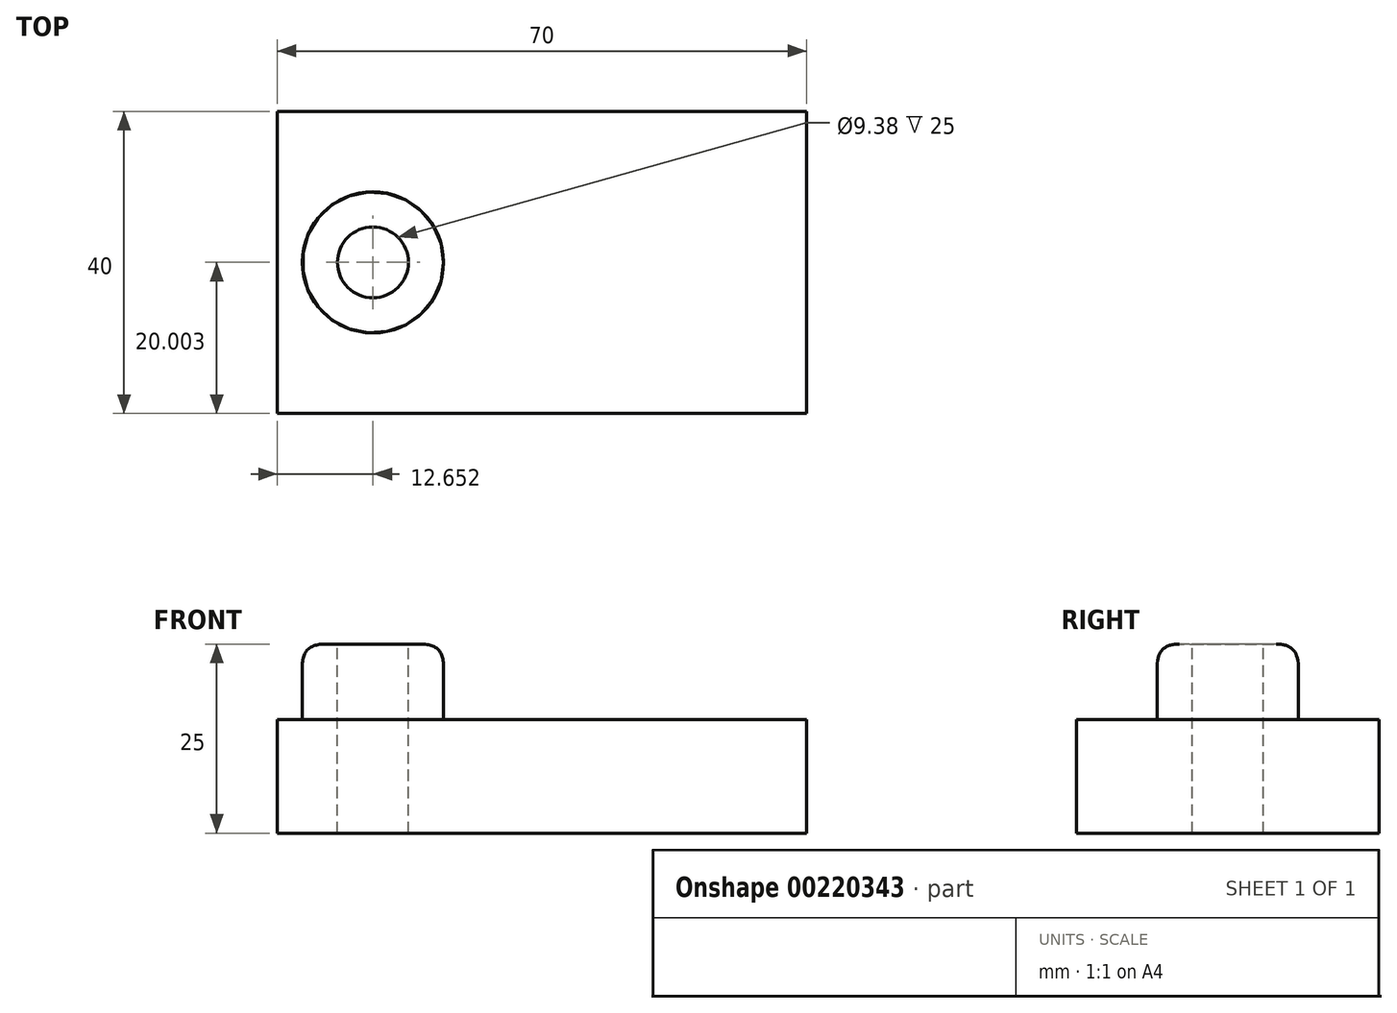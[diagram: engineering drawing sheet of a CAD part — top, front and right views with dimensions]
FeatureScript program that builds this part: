
annotation { "Feature Type Name" : "Feature", "Feature Type Description" : "" }
export const myFeature = defineFeature(function(context is Context, id is Id, definition is map)
    precondition{}
    {
        {
            var Q0;
            Q0=qCreatedBy(makeId("Top.planeOp"),FACE);
            var sketch = newSketch(context, id + "F0", { "sketchPlane" : qUnion([Q0])});
            skLineSegment(sketch, "E0.bottom", {"start": v(-41, 23.95) * mm, "end": v(29, 23.95) * mm});
            skLineSegment(sketch, "E0.top", {"start": v(-41, -16.05) * mm, "end": v(29, -16.05) * mm});
            skLineSegment(sketch, "E0.left", {"start": v(-41, 23.95) * mm, "end": v(-41, -16.05) * mm});
            skLineSegment(sketch, "E0.right", {"start": v(29, 23.95) * mm, "end": v(29, -16.05) * mm});
            skSolve(sketch);
        }
        {
            var Q0;
            Q0=makeQuery(id+"F0.imprint","IMPRINT",FACE,{"disambiguationData":[TD([[makeQuery(id+"F0.imprint","IMPRINT",EDGE,{"derivedFrom":sQuery(id+"F0.wireOp",EDGE,"E0.bottom")}),-1.0]])]});
            extrude(context, id + "F1", {"entities" : qUnion([Q0]), "depth" : 15 * mm});
        }
        {
            var Q0;
            Q0=makeQuery(id+"F1.opExtrude","CAP_FACE",FACE,{"disambiguationData":[OSD([sQuery(id+"F0.wireOp",EDGE,"E0.bottom"),sQuery(id+"F0.wireOp",EDGE,"E0.top"),sQuery(id+"F0.wireOp",EDGE,"E0.left"),sQuery(id+"F0.wireOp",EDGE,"E0.right")])],"isStart":false});
            cPlane(context, id + "F2", {"entities" : qUnion([Q0]), "cplaneType" : CPlaneType.OFFSET, "offset" : 0 * mm, "width" : 150 * mm, "height" : 150 * mm});
        }
        {
            var Q0;
            Q0=qCreatedBy(id+"F2.planeOp",FACE);
            var sketch = newSketch(context, id + "F3", { "sketchPlane" : qUnion([Q0])});
            skCircle(sketch, "E1", {"center": v(-28.35, 3.95) * mm, "radius": 9.33 * mm});
            skSolve(sketch);
        }
        {
            var Q0;
            Q0=makeQuery(id+"F3.imprint","IMPRINT",FACE,{"disambiguationData":[TD([[makeQuery(id+"F3.imprint","IMPRINT",EDGE,{"derivedFrom":sQuery(id+"F3.wireOp",EDGE,"E1")}),1.0]])]});
            extrude(context, id + "F4", {"entities" : qUnion([Q0]), "operationType" : NewBodyOperationType.ADD, "depth" : 10 * mm});
        }
        {
            var Q0;
            Q0=makeQuery(id+"F4.opExtrude","CAP_EDGE",EDGE,{"disambiguationData":[OSD([sQuery(id+"F3.wireOp",EDGE,"E1")])],"isStart":false});
            fillet(context, id + "F5", {"entities" : qUnion([Q0]), "radius" : 2.9 * mm, "rho" : 0.5, "crossSection" : FilletCrossSection.CONIC, "allowEdgeOverflow" : false});
        }
        {
            var Q0;
            Q0=makeQuery(id+"F4.opExtrude","CAP_FACE",FACE,{"disambiguationData":[OSD([sQuery(id+"F3.wireOp",EDGE,"E1")])],"isStart":false});
            cPlane(context, id + "F6", {"entities" : qUnion([Q0]), "cplaneType" : CPlaneType.OFFSET, "offset" : 0 * mm, "width" : 150 * mm, "height" : 150 * mm});
        }
        {
            var Q0;
            Q0=qCreatedBy(id+"F6.planeOp",FACE);
            var sketch = newSketch(context, id + "F7", { "sketchPlane" : qUnion([Q0])});
            skCircle(sketch, "E2", {"center": v(-28.35, 3.95) * mm, "radius": 4.69 * mm});
            skSolve(sketch);
        }
        {
            var Q0;
            Q0=makeQuery(id+"F7.imprint","IMPRINT",FACE,{"disambiguationData":[TD([[makeQuery(id+"F7.imprint","IMPRINT",EDGE,{"derivedFrom":sQuery(id+"F7.wireOp",EDGE,"E2")}),1.0]])]});
            extrude(context, id + "F8", {"entities" : qUnion([Q0]), "operationType" : NewBodyOperationType.REMOVE, "endBound" : BoundingType.THROUGH_ALL, "oppositeDirection" : true, "depth" : 25 * mm});
        }
    });
